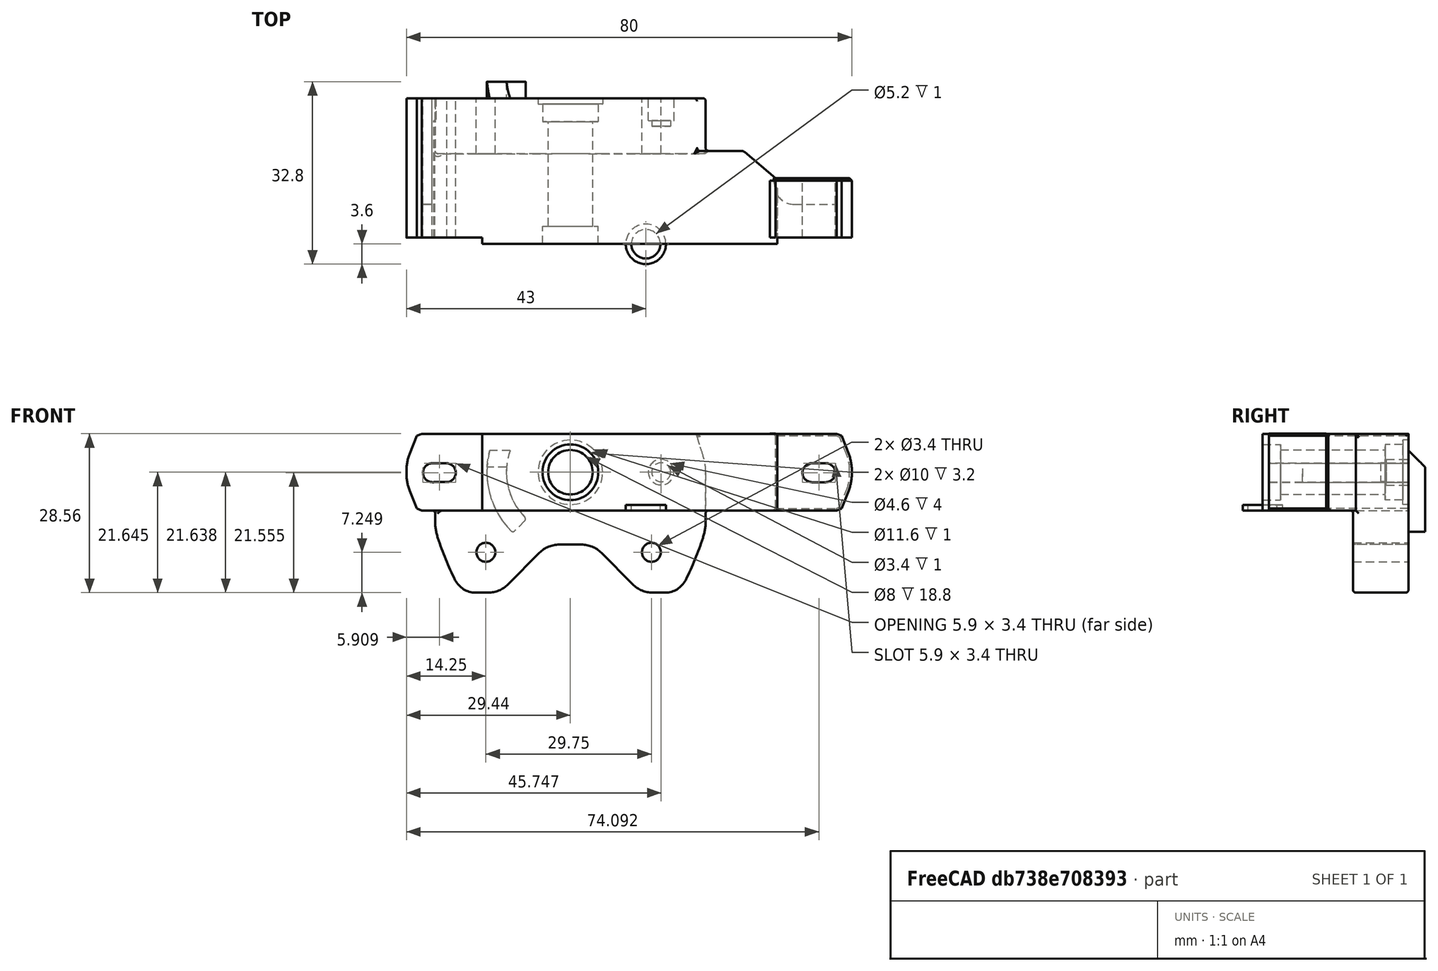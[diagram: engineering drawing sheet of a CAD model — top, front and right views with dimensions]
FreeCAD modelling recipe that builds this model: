
FCSTD DOCUMENT  (FreeCAD 0.18R16146 (Git))
Label: z-belt-bottom
License: All rights reserved
LicenseURL: http://en.wikipedia.org/wiki/All_rights_reserved
objects: Part::Feature×3, Part::Cut×3, Part::Box×2, Part::MultiFuse×2, Part::Cylinder×2, Part::Chamfer×1, App::Part×1
note: 13 computed .brp shape members not serialized (recipe doc carries the construction recipe); baked Part::Feature solids carry a one-line shape summary decoded from their .brp

FEATURE [Part::Feature] Part__Feature001  label="V0-ZBelt-FrontBottom-Bracket-ver1-Keyed-BETA2"
  Placement = pos=(-63,-154.7,147.42) rot=(0,0,1;0rad)
  shape: bbox 80.01 x 29.21 x 29.04 mm, 176 faces (baked)
FEATURE [Part::Box] Box  label="Cube"
  AttacherType = Attacher::AttachEngine3D
  Height = 13.81
  Length = 14.69
  Placement = pos=(22.31,1.15,0) rot=(0,0,1;0rad)
  Width = 10.66
FEATURE [Part::Box] Box001  label="Cube001"
  AttacherType = Attacher::AttachEngine3D
  Height = 13.81
  Length = 13.69
  Placement = pos=(23.31,1.15,0) rot=(0,0,1;0rad)
  Width = 5.66
FEATURE [Part::Feature] Part__Feature002  label="V0-ZBelt-FrontBottom-Bracket-ver1-Keyed-BETA003"
  Placement = pos=(-63,-154.7,147.42) rot=(0,0,1;0rad)
  shape: bbox 80.01 x 29.21 x 29.04 mm, 176 faces (baked)
FEATURE [Part::Cut] Cut
  Base = -> Box001
  Tool = -> Part__Feature002
FEATURE [Part::Feature] Cut001
  Placement = pos=(0,5,0) rot=(0,0,1;0rad)
  shape: bbox 13.69 x 5.66 x 13.81 mm, 22 faces, 3 solids (baked)
FEATURE [Part::MultiFuse] Fusion
  Shapes = -> [Cut001,Cut]
FEATURE [Part::Cut] Cut002
  Base = -> Box
  Tool = -> Fusion
FEATURE [Part::Chamfer] Chamfer
  Base = -> Cut002
  Edges = 12 edges r=0.4: [Edge3,Edge21,Edge25,Edge26,Edge27,Edge28,Edge29,Edge30,Edge31,Edge32,Edge33,Edge34]
FEATURE [Part::MultiFuse] Fusion001
  Shapes = -> [Chamfer,Part__Feature001]
FEATURE [App::Part] Part
  Group = -> [Fusion,Cut,Cut001,Box,Box001,Part__Feature002,Chamfer,Cut002,Part__Feature001,Fusion001]
  Origin = -> Origin
FEATURE [Part::Cylinder] Cylinder002
  Angle = 360
  AttacherType = Attacher::AttachEngine3D
  Height = 1
  Radius = 2.6
FEATURE [Part::Cylinder] Cylinder003
  Angle = 360
  AttacherType = Attacher::AttachEngine3D
  Height = 1
  Radius = 3.6
FEATURE [Part::Cut] Cut003  label="1mm-spacer"
  Base = -> Cylinder003
  Tool = -> Cylinder002
